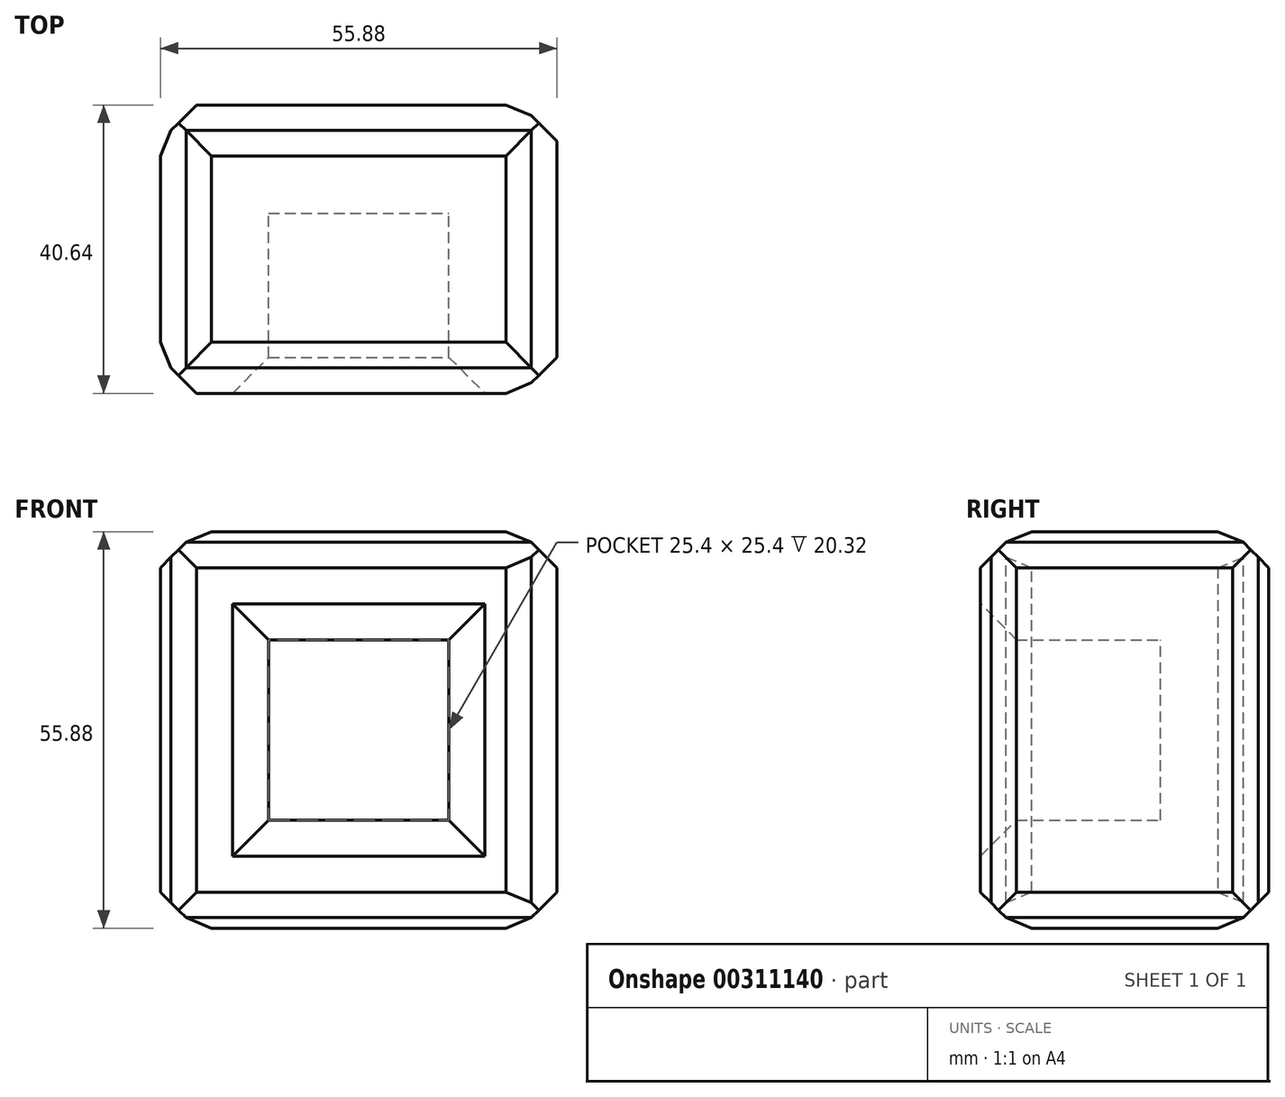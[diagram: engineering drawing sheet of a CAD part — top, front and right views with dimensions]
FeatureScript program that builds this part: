
annotation { "Feature Type Name" : "Feature", "Feature Type Description" : "" }
export const myFeature = defineFeature(function(context is Context, id is Id, definition is map)
    precondition{}
    {
        {
            var Q0;
            Q0=qCreatedBy(makeId("Front.planeOp"),FACE);
            var sketch = newSketch(context, id + "F0", { "sketchPlane" : qUnion([Q0])});
            skLineSegment(sketch, "E0.bottom", {"start": v(0, 0) * mm, "end": v(25.4, 0) * mm});
            skLineSegment(sketch, "E0.top", {"start": v(0, 25.4) * mm, "end": v(25.4, 25.4) * mm});
            skLineSegment(sketch, "E0.left", {"start": v(0, 0) * mm, "end": v(0, 25.4) * mm});
            skLineSegment(sketch, "E0.right", {"start": v(25.4, 0) * mm, "end": v(25.4, 25.4) * mm});
            skSolve(sketch);
        }
        {
            var Q0;
            Q0 = qSketchRegion(id + "F0", true);
            extrude(context, id + "F1", {"entities" : qUnion([Q0]), "depth" : 25.4 * mm});
        }
        {
            var Q0;
            Q0=makeQuery(id+"F1.opExtrude","CAP_FACE",FACE,{"disambiguationData":[OSD([sQuery(id+"F0.wireOp",EDGE,"E0.bottom"),sQuery(id+"F0.wireOp",EDGE,"E0.top"),sQuery(id+"F0.wireOp",EDGE,"E0.left"),sQuery(id+"F0.wireOp",EDGE,"E0.right")])],"isStart":false});
            shell(context, id + "F2", {"entities" : qUnion([Q0]), "thickness" : 15.24 * mm, "oppositeDirection" : true});
        }
        {
            var Q0;
            Q0=makeQuery(id+"F1.opExtrude","SWEPT_FACE",FACE,{"disambiguationData":[OSD([sQuery(id+"F0.wireOp",EDGE,"E0.right")])]});
            chamfer(context, id + "F3", {"entities" : qUnion([Q0]), "width" : 5.08 * mm, "tangentPropagation" : true});
        }
        {
            var Q0;
            Q0=makeQuery(id+"F1.opExtrude","CAP_FACE",FACE,{"disambiguationData":[OSD([sQuery(id+"F0.wireOp",EDGE,"E0.bottom"),sQuery(id+"F0.wireOp",EDGE,"E0.top"),sQuery(id+"F0.wireOp",EDGE,"E0.left"),sQuery(id+"F0.wireOp",EDGE,"E0.right")])],"isStart":true});
            chamfer(context, id + "F4", {"entities" : qUnion([Q0]), "width" : 5.08 * mm, "tangentPropagation" : true});
        }
        {
            var Q0;
            Q0=makeQuery(id+"F1.opExtrude","CAP_FACE",FACE,{"disambiguationData":[OSD([sQuery(id+"F0.wireOp",EDGE,"E0.bottom"),sQuery(id+"F0.wireOp",EDGE,"E0.top"),sQuery(id+"F0.wireOp",EDGE,"E0.left"),sQuery(id+"F0.wireOp",EDGE,"E0.right")])],"isStart":false});
            chamfer(context, id + "F5", {"entities" : qUnion([Q0]), "width" : 5.08 * mm, "tangentPropagation" : true});
        }
        {
            var Q0;
            Q0=makeQuery(id+"F1.opExtrude","SWEPT_FACE",FACE,{"disambiguationData":[OSD([sQuery(id+"F0.wireOp",EDGE,"E0.left")])]});
            chamfer(context, id + "F6", {"entities" : qUnion([Q0]), "width" : 5.08 * mm, "tangentPropagation" : true});
        }
        {
            var Q0;
            Q0=makeQuery(id+"F1.opExtrude","SWEPT_FACE",FACE,{"disambiguationData":[OSD([sQuery(id+"F0.wireOp",EDGE,"E0.top")])]});
            chamfer(context, id + "F7", {"entities" : qUnion([Q0]), "width" : 5.08 * mm, "tangentPropagation" : true});
        }
        {
            var Q0;
            Q0=makeQuery(id+"F1.opExtrude","SWEPT_FACE",FACE,{"disambiguationData":[OSD([sQuery(id+"F0.wireOp",EDGE,"E0.bottom")])]});
            chamfer(context, id + "F8", {"entities" : qUnion([Q0]), "width" : 5.08 * mm, "tangentPropagation" : true});
        }
    });
